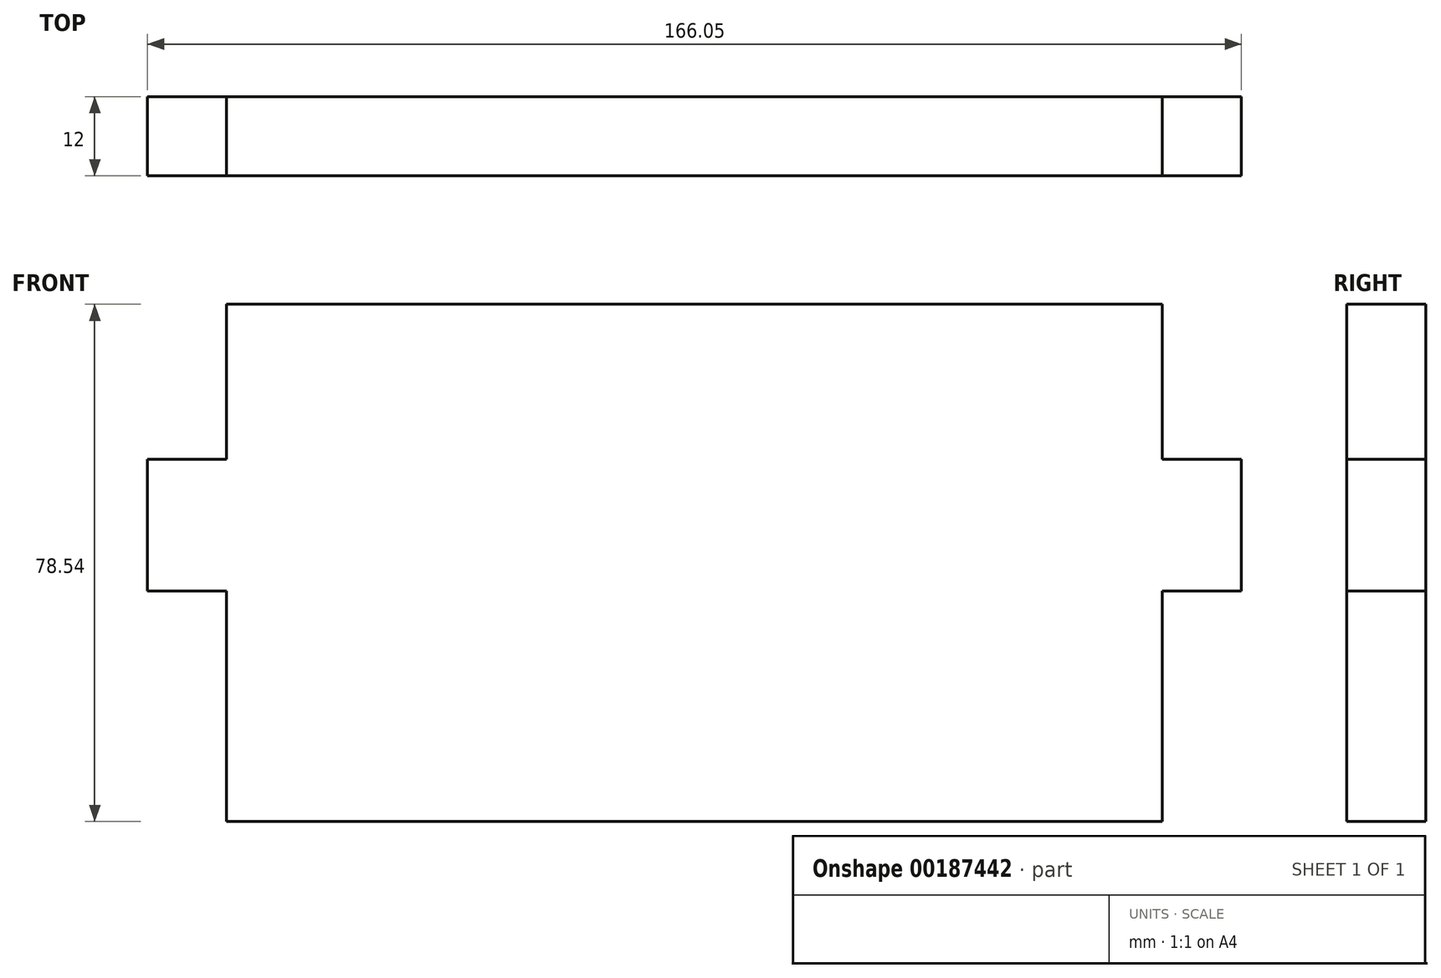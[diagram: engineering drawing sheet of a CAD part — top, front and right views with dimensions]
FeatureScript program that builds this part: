
annotation { "Feature Type Name" : "Feature", "Feature Type Description" : "" }
export const myFeature = defineFeature(function(context is Context, id is Id, definition is map)
    precondition{}
    {
        {
            var Q0;
            Q0=qCreatedBy(makeId("Front.planeOp"),FACE);
            var sketch = newSketch(context, id + "F0", { "sketchPlane" : qUnion([Q0])});
            skLineSegment(sketch, "E0.bottom", {"start": v(0, 0) * mm, "end": v(142.05, 0) * mm});
            skLineSegment(sketch, "E0.top", {"start": v(0, 90) * mm, "end": v(142.05, 90) * mm});
            skLineSegment(sketch, "E0.left", {"start": v(0, 0) * mm, "end": v(0, 90) * mm});
            skLineSegment(sketch, "E0.right", {"start": v(142.05, 0) * mm, "end": v(142.05, 90) * mm});
            skSolve(sketch);
        }
        {
            var Q0;
            Q0 = qSketchRegion(id + "F0", true);
            extrude(context, id + "F1", {"entities" : qUnion([Q0]), "offsetDistance" : 25 * mm, "depth" : 12 * mm});
        }
        {
            var Q0;
            Q0=makeQuery(id+"F1.opExtrude","CAP_FACE",FACE,{"disambiguationData":[OSD([sQuery(id+"F0.wireOp",EDGE,"E0.bottom"),sQuery(id+"F0.wireOp",EDGE,"E0.top"),sQuery(id+"F0.wireOp",EDGE,"E0.left"),sQuery(id+"F0.wireOp",EDGE,"E0.right")])],"isStart":false});
            var sketch = newSketch(context, id + "F2", { "sketchPlane" : qUnion([Q0])});
            skLineSegment(sketch, "E1.bottom", {"start": v(12, 55) * mm, "end": v(-12, 55) * mm});
            skLineSegment(sketch, "E1.top", {"start": v(12, 35) * mm, "end": v(-12, 35) * mm});
            skLineSegment(sketch, "E1.left", {"start": v(12, 55) * mm, "end": v(12, 35) * mm});
            skLineSegment(sketch, "E1.right", {"start": v(-12, 55) * mm, "end": v(-12, 35) * mm});
            skPoint(sketch, "E1.middle", {"position": v(0, 45) * mm});
            skLineSegment(sketch, "E2.bottom", {"start": v(154.05, 55) * mm, "end": v(130.05, 55) * mm});
            skLineSegment(sketch, "E2.top", {"start": v(154.05, 35) * mm, "end": v(130.05, 35) * mm});
            skLineSegment(sketch, "E2.left", {"start": v(154.05, 55) * mm, "end": v(154.05, 35) * mm});
            skLineSegment(sketch, "E2.right", {"start": v(130.05, 55) * mm, "end": v(130.05, 35) * mm});
            skPoint(sketch, "E2.middle", {"position": v(142.05, 45) * mm});
            skSolve(sketch);
        }
        {
            var Q0;
            Q0 = qSketchRegion(id + "F2", true);
            extrude(context, id + "F3", {"entities" : qUnion([Q0]), "operationType" : NewBodyOperationType.ADD, "oppositeDirection" : true, "depth" : 12 * mm, "offsetDistance" : 25 * mm});
        }
        {
            var Q0;
            Q0=makeQuery(id+"F1.opExtrude","SWEPT_FACE",FACE,{"disambiguationData":[OSD([sQuery(id+"F0.wireOp",EDGE,"E0.top")])]});
            extrude(context, id + "F4", {"entities" : qUnion([Q0]), "operationType" : NewBodyOperationType.REMOVE, "oppositeDirection" : true, "depth" : 10.03 * mm, "offsetDistance" : 25 * mm});
        }
        {
            var Q0;
            Q0=makeQuery(id+"F3.boolean.opBoolean","MERGE",FACE,{"derivedFrom":[makeQuery(id+"F1.opExtrude","CAP_FACE",FACE,{"disambiguationData":[OSD([sQuery(id+"F0.wireOp",EDGE,"E0.bottom"),sQuery(id+"F0.wireOp",EDGE,"E0.top"),sQuery(id+"F0.wireOp",EDGE,"E0.left"),sQuery(id+"F0.wireOp",EDGE,"E0.right")])],"isStart":false}),makeQuery(id+"F3.opExtrude","CAP_FACE",FACE,{"disambiguationData":[OSD([sQuery(id+"F2.wireOp",EDGE,"E1.bottom"),sQuery(id+"F2.wireOp",EDGE,"E1.top"),sQuery(id+"F2.wireOp",EDGE,"E1.left"),sQuery(id+"F2.wireOp",EDGE,"E1.right")])],"isStart":true}),makeQuery(id+"F3.opExtrude","CAP_FACE",FACE,{"disambiguationData":[OSD([sQuery(id+"F2.wireOp",EDGE,"E2.bottom"),sQuery(id+"F2.wireOp",EDGE,"E2.top"),sQuery(id+"F2.wireOp",EDGE,"E2.left"),sQuery(id+"F2.wireOp",EDGE,"E2.right")])],"isStart":true})]});
            var sketch = newSketch(context, id + "F5", { "sketchPlane" : qUnion([Q0])});
            skLineSegment(sketch, "E3", {"start": v(0, 78.54) * mm, "end": v(142.05, 78.54) * mm});
            skSolve(sketch);
        }
        {
            var Q0;
            {var subQ0=sQuery(id+"F5.wireOp",EDGE,"E3");Q0=makeQuery(id+"F5.imprint","IMPRINT",FACE,{"disambiguationData":[TD([[makeQuery(id+"F5.imprint","IMPRINT",EDGE,{"derivedFrom":subQ0}),1.0]])]});}
            extrude(context, id + "F6", {"entities" : qUnion([Q0]), "operationType" : NewBodyOperationType.REMOVE, "oppositeDirection" : true, "depth" : 25 * mm, "offsetDistance" : 25 * mm});
        }
    });
